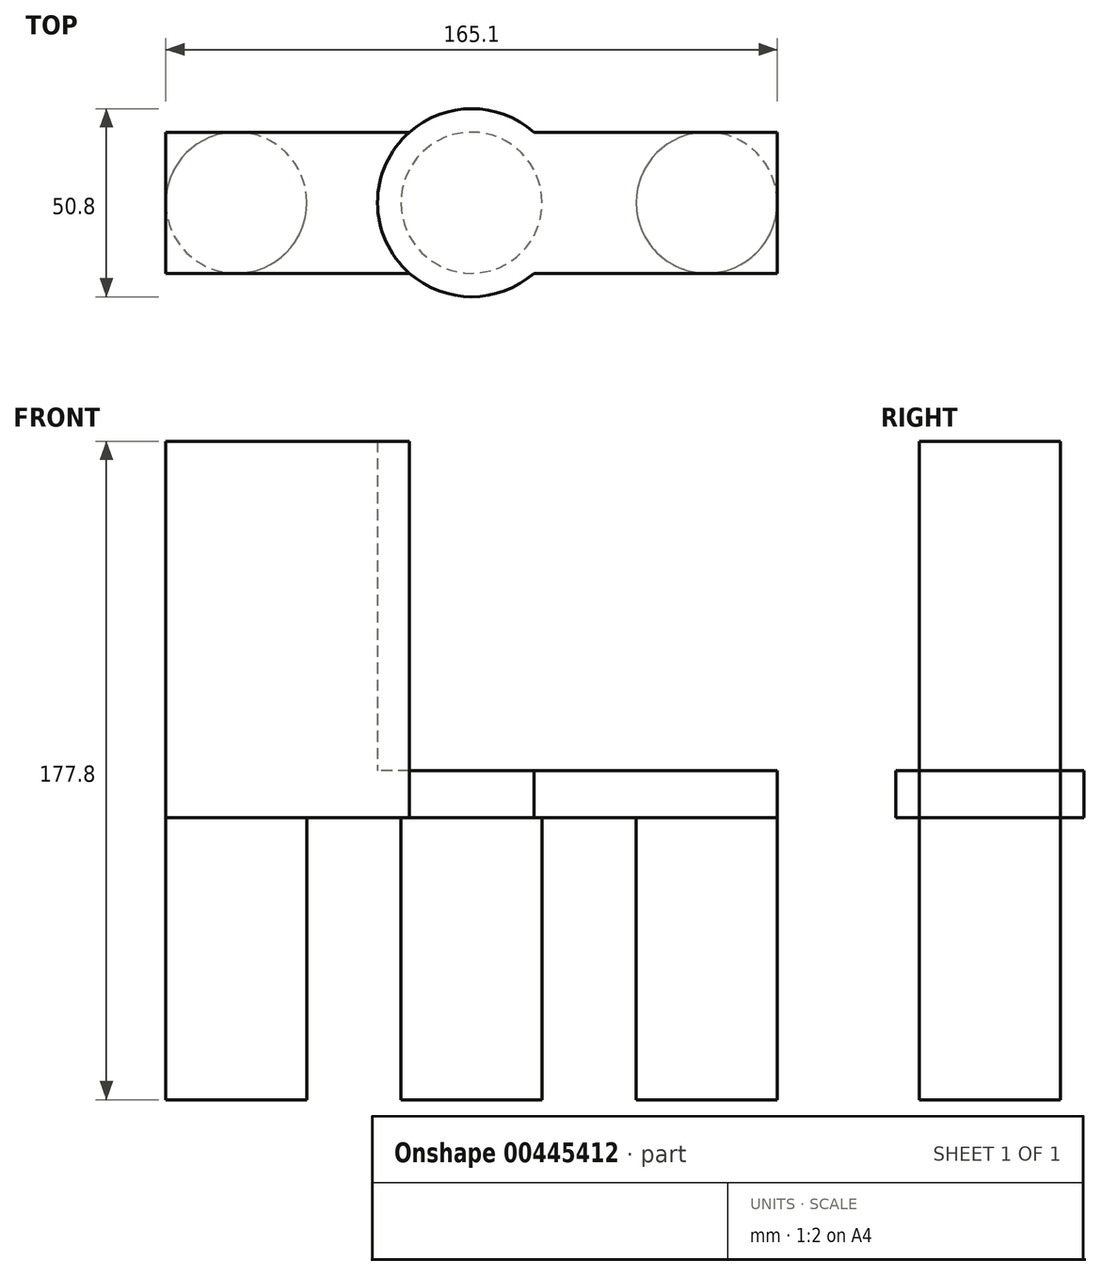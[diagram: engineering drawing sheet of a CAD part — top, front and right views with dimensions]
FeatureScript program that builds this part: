
annotation { "Feature Type Name" : "Feature", "Feature Type Description" : "" }
export const myFeature = defineFeature(function(context is Context, id is Id, definition is map)
    precondition{}
    {
        {
            var Q0;
            Q0=qCreatedBy(makeId("Top.planeOp"),FACE);
            var sketch = newSketch(context, id + "F0", { "sketchPlane" : qUnion([Q0])});
            skLineSegment(sketch, "E0.bottom", {"start": v(82.55, 19.05) * mm, "end": v(-82.55, 19.05) * mm});
            skLineSegment(sketch, "E0.top", {"start": v(82.55, -19.05) * mm, "end": v(-82.55, -19.05) * mm});
            skLineSegment(sketch, "E0.left", {"start": v(82.55, 19.05) * mm, "end": v(82.55, -19.05) * mm});
            skLineSegment(sketch, "E0.right", {"start": v(-82.55, 19.05) * mm, "end": v(-82.55, -19.05) * mm});
            skPoint(sketch, "E0.middle", {"position": v(0, 0) * mm});
            skCircle(sketch, "E1", {"center": v(0, 0) * mm, "radius": 25.4 * mm});
            skSolve(sketch);
        }
        {
            var Q0;
            {var subQ0=sQuery(id+"F0.wireOp",EDGE,"E1");var subQ1=sQuery(id+"F0.wireOp",EDGE,"E0.top");var subQ2=makeQuery(id+"F0.imprint","INTERSECT",VERTEX,{"disambiguationData":[OD(0.0)],"derivedFrom":[subQ1,subQ0]});Q0=makeQuery(id+"F0.imprint","IMPRINT",FACE,{"disambiguationData":[TD([[makeQuery(id+"F0.imprint","IMPRINT",EDGE,{"disambiguationData":[TD([[subQ2,-1.0]])],"derivedFrom":subQ1}),1.0]])]});}
            var Q1;
            {var subQ0=sQuery(id+"F0.wireOp",EDGE,"E1");var subQ1=sQuery(id+"F0.wireOp",EDGE,"E0.bottom");var subQ2=makeQuery(id+"F0.imprint","INTERSECT",VERTEX,{"disambiguationData":[OD(0.0)],"derivedFrom":[subQ1,subQ0]});Q1=makeQuery(id+"F0.imprint","IMPRINT",FACE,{"disambiguationData":[TD([[makeQuery(id+"F0.imprint","IMPRINT",EDGE,{"disambiguationData":[TD([[subQ2,-1.0]])],"derivedFrom":subQ1}),1.0]])]});}
            var Q2;
            {var subQ0=sQuery(id+"F0.wireOp",EDGE,"E1");var subQ1=sQuery(id+"F0.wireOp",EDGE,"E0.bottom");var subQ2=makeQuery(id+"F0.imprint","INTERSECT",VERTEX,{"disambiguationData":[OD(0.0)],"derivedFrom":[subQ1,subQ0]});Q2=makeQuery(id+"F0.imprint","IMPRINT",FACE,{"disambiguationData":[TD([[makeQuery(id+"F0.imprint","IMPRINT",EDGE,{"disambiguationData":[TD([[subQ2,-1.0]])],"derivedFrom":subQ1}),-1.0]])]});}
            extrude(context, id + "F1", {"entities" : qUnion([Q0, Q1, Q2]), "depth" : 101.6 * mm});
        }
        {
            var Q0;
            Q0 = qSketchRegion(id + "F0", true);
            extrude(context, id + "F2", {"entities" : qUnion([Q0]), "operationType" : NewBodyOperationType.ADD, "depth" : 12.7 * mm});
        }
        {
            var Q0;
            Q0=qCreatedBy(makeId("Top.planeOp"),FACE);
            var sketch = newSketch(context, id + "F3", { "sketchPlane" : qUnion([Q0])});
            skCircle(sketch, "E2", {"center": v(0, 0) * mm, "radius": 19.05 * mm});
            skLineSegment(sketch, "E3", {"start": v(0, 0) * mm, "end": v(-82.55, 0) * mm});
            skLineSegment(sketch, "E4", {"start": v(0, 0) * mm, "end": v(82.55, 0) * mm});
            skLineSegment(sketch, "E5", {"start": v(-82.55, 0) * mm, "end": v(-63.5, 0) * mm});
            skCircle(sketch, "E6", {"center": v(-63.5, 0) * mm, "radius": 19.05 * mm});
            skLineSegment(sketch, "E7", {"start": v(82.55, 0) * mm, "end": v(63.5, 0) * mm});
            skCircle(sketch, "E8", {"center": v(63.5, 0) * mm, "radius": 19.05 * mm});
            skSolve(sketch);
        }
        {
            var Q0;
            Q0 = qSketchRegion(id + "F3", true);
            extrude(context, id + "F4", {"entities" : qUnion([Q0]), "operationType" : NewBodyOperationType.ADD, "oppositeDirection" : true, "depth" : 76.2 * mm});
        }
    });
